# Revit family: IS_Tesi_T3546_BIM_BE
name_source: partatom
category: Plumbing Fixtures
revit_build: Autodesk Revit 2015 (Build: 20140606_1530(x64)
units: mm (PartAtom-declared; Revit-internal decimal feet)

## types (1)
- T354601 - Tesi PACK WC suspendu AquaBlade® avec abattant et couvercle fin slow closing, fixation invisible (set de fixation inclus)
    Accesoires = www.idealstandard.be
    Afwerking = Wit
    Auteur = Ideal Standard Produktions-GmbH
    Barcode = 8014140430506
    Beschrijvinggarantie = Fabrieksgarantie
    BimObjectNaam = ISI_IdealStandard_WC_Tesi_T354601
    Breedte = 0
    BrutoGewicht = 0
    Cost = 0 $
    Default Elevation = 400 mm
    Description = Tesi PACK WC suspendu AquaBlade® avec abattant et couvercle fin slow closing, fixation invisible (set de fixation inclus)
    Diepte = 0 mm  [stored 0 ft]
    Dimensions = 530 x 360 x 337 mm
    DuurEenheid = jaar
    Eigenschappen = PACK Tesi wand-WC met Aquablade® spoeltechnologie, met
verborgen bevestiging. DIN EN997. Volledig geglazuurd. Met dunne
zitting en deksel slow closing (easy take-off).
    Garantieonderdelen = 10
    Hauteur = 337 mm
    IfcExportAs = IfcSanitaryTerminalType
    IfcExportType = TOILETPANS
    Installatieinstructies = www.idealstandard.be
    Kleur = Wit
    Kleurwc = Wit
    Largeur = 360 mm
    Lengte = 0 mm  [stored 0 ft]
    Longueur = 530 mm
    Manufacturer = www.idealstandard.be
    Materiaal = porselein
    MateriaalWC = porselein
    Merk = Ideal Standard
    Model = T354601
    Nettogewicht = 22
    Normen = DIN EN997
    Overloop = 0 mm  [stored 0 ft]
    Productinformatie = www.idealstandard.be
    Telefoonnummer = 0032 2 325 66 00
    Testdruk = 0
    TypeWC = Wand-WC
    Typeconnectie = Sanitair
    TypespoelingWC = Diepspoel
    URL = www.idealstandard.be
    Uniclass2015Beschrijving = WC pans
    Uniclass2015Referentie = Pr_40_20_93_94
    Uniclass2015Version = Products v1.1
    Urlproducent = www.idealstandard.be
    Versie = 1
    Vervangingskosten = 0
    Verwachtelevensduur = 25 jaar
    Volumeunits = liter

note: [stored X ft] marks values corroborated as IEEE doubles in the binary element streams (Revit-internal decimal feet)

## geometry (parser evidence)
native form markers: Blend x4, Sweep x1
no freeform markers — native parametric forms only
